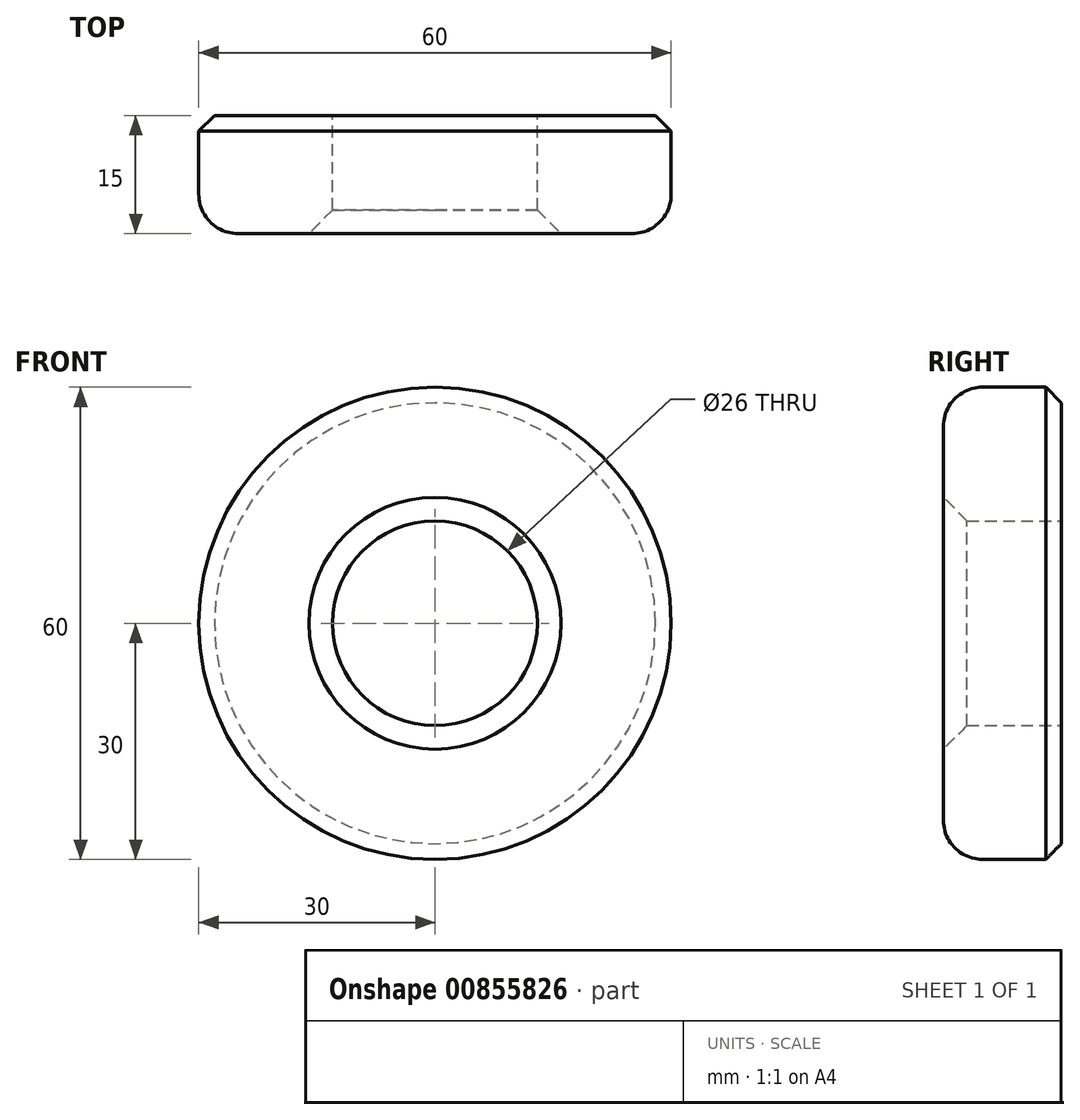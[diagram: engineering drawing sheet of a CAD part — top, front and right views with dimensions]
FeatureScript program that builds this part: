
annotation { "Feature Type Name" : "Feature", "Feature Type Description" : "" }
export const myFeature = defineFeature(function(context is Context, id is Id, definition is map)
    precondition{}
    {
        {
            var Q0;
            Q0=qCreatedBy(makeId("Front.planeOp"),FACE);
            var sketch = newSketch(context, id + "F0", { "sketchPlane" : qUnion([Q0])});
            skCircle(sketch, "E0", {"center": v(0, 0) * mm, "radius": 13 * mm});
            skCircle(sketch, "E1", {"center": v(0, 0) * mm, "radius": 30 * mm});
            skSolve(sketch);
        }
        {
            var Q0;
            Q0 = qSketchRegion(id + "F0", true);
            extrude(context, id + "F1", {"entities" : qUnion([Q0]), "depth" : 15 * mm, "offsetDistance" : 25 * mm});
        }
        {
            var Q0;
            Q0=makeQuery(id+"F1.opExtrude","CAP_EDGE",EDGE,{"disambiguationData":[OSD([sQuery(id+"F0.wireOp",EDGE,"E1")])],"isStart":false});
            fillet(context, id + "F2", {"entities" : qUnion([Q0]), "radius" : 5 * mm, "tangentPropagation" : true, "allowEdgeOverflow" : false});
        }
        {
            var Q0;
            Q0=makeQuery(id+"F1.opExtrude","CAP_EDGE",EDGE,{"disambiguationData":[OSD([sQuery(id+"F0.wireOp",EDGE,"E0")])],"isStart":false});
            chamfer(context, id + "F3", {"entities" : qUnion([Q0]), "width" : 3 * mm, "tangentPropagation" : true});
        }
        {
            var Q0;
            Q0=makeQuery(id+"F1.opExtrude","CAP_EDGE",EDGE,{"disambiguationData":[OSD([sQuery(id+"F0.wireOp",EDGE,"E1")])],"isStart":true});
            chamfer(context, id + "F4", {"entities" : qUnion([Q0]), "width" : 2 * mm, "tangentPropagation" : true});
        }
    });
